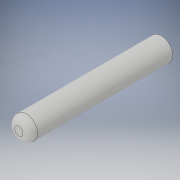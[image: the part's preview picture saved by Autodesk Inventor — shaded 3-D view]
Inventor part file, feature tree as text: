
AUTODESK INVENTOR PART (.ipt)
format: ipt  version: 2019 (Build 230136000, 136)  size: 99,840 bytes
history: native  units: mm
features: extrude x1, fillet x1, sketch x1
ambient origin geometry x8: Origin, YZ Plane, XZ Plane, XY Plane, X Axis, Y Axis, Z Axis, Center Point
bodies: Solid1 (feature_tree)
feature tree (3):
  extrude  "Extrusion1"  Depth=484.0mm TaperAngle=0.0deg
  fillet  "Fillet1"  Radius=25.0mm
  sketch  "Sketch1"  dims[d0=78.0mm d1=484.0mm d2=0.0mm d3=25.0mm]
